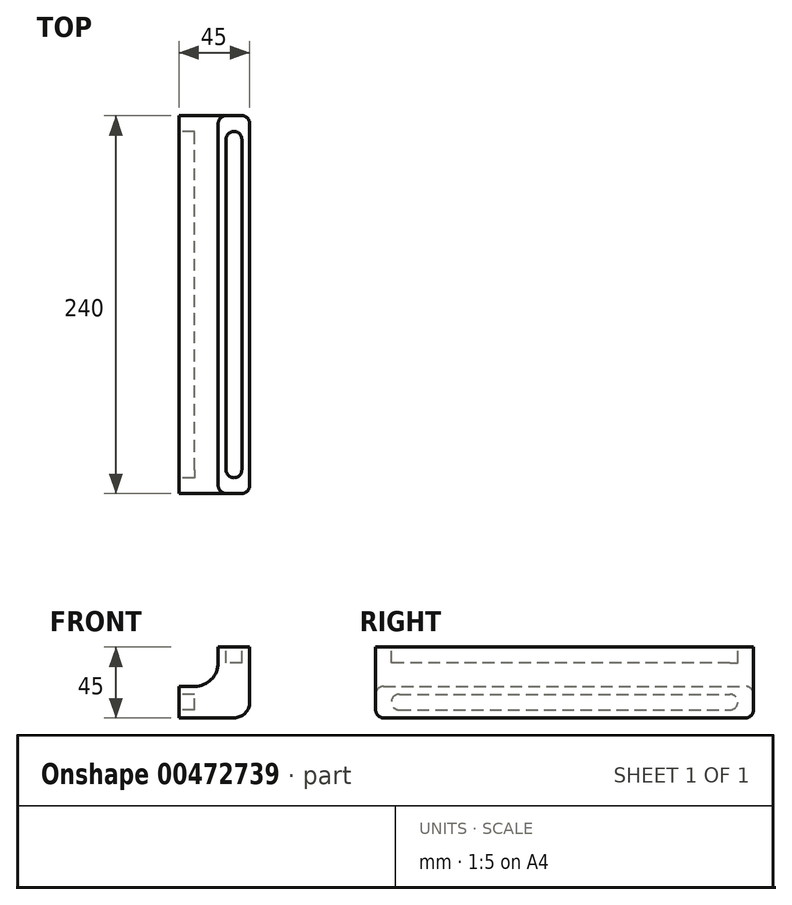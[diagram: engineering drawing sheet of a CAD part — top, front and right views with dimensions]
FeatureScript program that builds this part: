
annotation { "Feature Type Name" : "Feature", "Feature Type Description" : "" }
export const myFeature = defineFeature(function(context is Context, id is Id, definition is map)
    precondition{}
    {
        {
            var Q0;
            Q0=qCreatedBy(makeId("Front.planeOp"),FACE);
            var sketch = newSketch(context, id + "F0", { "sketchPlane" : qUnion([Q0])});
            skLineSegment(sketch, "E0.bottom", {"start": v(22.5, -22.5) * mm, "end": v(-22.5, -22.5) * mm});
            skLineSegment(sketch, "E0.top", {"start": v(22.5, 22.5) * mm, "end": v(2.5, 22.5) * mm});
            skLineSegment(sketch, "E0.left", {"start": v(22.5, -22.5) * mm, "end": v(22.5, 22.5) * mm});
            skLineSegment(sketch, "E0.right", {"start": v(-22.5, -22.5) * mm, "end": v(-22.5, -2.5) * mm});
            skPoint(sketch, "E0.middle", {"position": v(0, 0) * mm});
            skLineSegment(sketch, "E1", {"start": v(0, 22.5) * mm, "end": v(0, -22.5) * mm, "construction": true});
            skLineSegment(sketch, "E2", {"start": v(-22.5, 0) * mm, "end": v(22.5, 0) * mm, "construction": true});
            skLineSegment(sketch, "E3.0", {"start": v(2.5, -2.5) * mm, "end": v(-22.5, -2.5) * mm});
            skPoint(sketch, "E4.orphan", {"position": v(-22.5, 22.5) * mm});
            skLineSegment(sketch, "E5.trimOffspring", {"start": v(2.5, -2.5) * mm, "end": v(2.5, 22.5) * mm});
            skSolve(sketch);
        }
        {
            var Q0;
            Q0 = qSketchRegion(id + "F0", true);
            extrude(context, id + "F1", {"entities" : qUnion([Q0]), "depth" : 240 * mm, "offsetDistance" : 25 * mm});
        }
        {
            var Q0;
            Q0=makeQuery(id+"F1.opExtrude","SWEPT_EDGE",EDGE,{"disambiguationData":[OSD([sQuery(id+"F0.wireOp",EDGE,"E3.0"),sQuery(id+"F0.wireOp",EDGE,"E5.trimOffspring")])]});
            fillet(context, id + "F2", {"entities" : qUnion([Q0]), "radius" : 15 * mm, "tangentPropagation" : true, "allowEdgeOverflow" : false});
        }
        {
            var Q0;
            Q0=makeQuery(id+"F1.opExtrude","SWEPT_EDGE",EDGE,{"disambiguationData":[OSD([sQuery(id+"F0.wireOp",EDGE,"E0.bottom"),sQuery(id+"F0.wireOp",EDGE,"E0.left")])]});
            fillet(context, id + "F3", {"entities" : qUnion([Q0]), "radius" : 10 * mm, "tangentPropagation" : true, "allowEdgeOverflow" : false});
        }
        {
            var Q0;
            Q0=makeQuery(id+"F1.opExtrude","SWEPT_FACE",FACE,{"disambiguationData":[OSD([sQuery(id+"F0.wireOp",EDGE,"E0.top")])]});
            var sketch = newSketch(context, id + "F4", { "sketchPlane" : qUnion([Q0])});
            skLineSegment(sketch, "E6", {"start": v(12.5, -240) * mm, "end": v(12.5, 0) * mm, "construction": true});
            skLineSegment(sketch, "E7", {"start": v(2.5, -120) * mm, "end": v(22.5, -120) * mm, "construction": true});
            skArc(sketch, "E8", {"start": v(7.5, -225) * mm, "mid": v(12.5, -230) * mm, "end": v(17.5, -225) * mm});
            skArc(sketch, "E9.MirrorC", {"start": v(7.5, -15) * mm, "mid": v(12.5, -10) * mm, "end": v(17.5, -15) * mm});
            skLineSegment(sketch, "E10", {"start": v(7.5, -15) * mm, "end": v(7.5, -225) * mm});
            skLineSegment(sketch, "E11.MirrorCS", {"start": v(17.5, -15) * mm, "end": v(17.5, -225) * mm});
            skSolve(sketch);
        }
        {
            var Q0;
            Q0 = qSketchRegion(id + "F4", true);
            extrude(context, id + "F5", {"entities" : qUnion([Q0]), "operationType" : NewBodyOperationType.REMOVE, "oppositeDirection" : true, "depth" : 10 * mm, "offsetDistance" : 25 * mm});
        }
        {
            var Q0;
            Q0=makeQuery(id+"F1.opExtrude","SWEPT_FACE",FACE,{"disambiguationData":[OSD([sQuery(id+"F0.wireOp",EDGE,"E0.right")])]});
            var sketch = newSketch(context, id + "F6", { "sketchPlane" : qUnion([Q0])});
            skLineSegment(sketch, "E12", {"start": v(240, -12.5) * mm, "end": v(0, -12.5) * mm, "construction": true});
            skLineSegment(sketch, "E13", {"start": v(120, -2.5) * mm, "end": v(120, -22.5) * mm, "construction": true});
            skArc(sketch, "E14", {"start": v(15, -7.5) * mm, "mid": v(10, -12.5) * mm, "end": v(15, -17.5) * mm});
            skArc(sketch, "E15.MirrorC", {"start": v(225, -7.5) * mm, "mid": v(230, -12.5) * mm, "end": v(225, -17.5) * mm});
            skLineSegment(sketch, "E16", {"start": v(225, -7.5) * mm, "end": v(15, -7.5) * mm});
            skLineSegment(sketch, "E17.MirrorCS", {"start": v(225, -17.5) * mm, "end": v(15, -17.5) * mm});
            skSolve(sketch);
        }
        {
            var Q0;
            Q0 = qSketchRegion(id + "F6", true);
            extrude(context, id + "F7", {"entities" : qUnion([Q0]), "operationType" : NewBodyOperationType.REMOVE, "oppositeDirection" : true, "depth" : 10 * mm, "offsetDistance" : 25 * mm});
        }
        {
            var Q0;
            Q0=makeQuery(id+"F1.opExtrude","CAP_EDGE",EDGE,{"disambiguationData":[OSD([sQuery(id+"F0.wireOp",EDGE,"E0.left")])],"isStart":false});
            var Q1;
            {var subQ0=sQuery(id+"F0.wireOp",EDGE,"E0.left");var subQ1=sQuery(id+"F0.wireOp",EDGE,"E0.bottom");Q1=makeQuery(id+"F3.opFillet","BLEND_EDGE",EDGE,{"blendedFrom":[makeQuery(id+"F1.opExtrude","SWEPT_EDGE",EDGE,{"disambiguationData":[OSD([subQ1,subQ0])]}),makeQuery(id+"F1.opExtrude","CAP_FACE",FACE,{"disambiguationData":[OSD([subQ1,sQuery(id+"F0.wireOp",EDGE,"E0.top"),subQ0,sQuery(id+"F0.wireOp",EDGE,"E0.right"),sQuery(id+"F0.wireOp",EDGE,"E3.0"),sQuery(id+"F0.wireOp",EDGE,"E5.trimOffspring")])],"isStart":false})],"blendedInto":[makeQuery(id+"F1.opExtrude","CAP_FACE",FACE,{"disambiguationData":[OSD([subQ1,sQuery(id+"F0.wireOp",EDGE,"E0.top"),subQ0,sQuery(id+"F0.wireOp",EDGE,"E0.right"),sQuery(id+"F0.wireOp",EDGE,"E3.0"),sQuery(id+"F0.wireOp",EDGE,"E5.trimOffspring")])],"isStart":false})]});}
            fillet(context, id + "F8", {"entities" : qUnion([Q0, Q1]), "radius" : 5 * mm, "tangentPropagation" : true, "allowEdgeOverflow" : false});
        }
        {
            var Q0;
            Q0=makeQuery(id+"F1.opExtrude","CAP_EDGE",EDGE,{"disambiguationData":[OSD([sQuery(id+"F0.wireOp",EDGE,"E0.left")])],"isStart":true});
            fillet(context, id + "F9", {"entities" : qUnion([Q0]), "radius" : 5 * mm, "tangentPropagation" : true, "allowEdgeOverflow" : false});
        }
        {
            var Q0;
            {var subQ0=sQuery(id+"F0.wireOp",EDGE,"E5.trimOffspring");var subQ1=sQuery(id+"F0.wireOp",EDGE,"E3.0");Q0=makeQuery(id+"F2.opFillet","BLEND_EDGE",EDGE,{"blendedFrom":[makeQuery(id+"F1.opExtrude","SWEPT_EDGE",EDGE,{"disambiguationData":[OSD([subQ1,subQ0])]}),makeQuery(id+"F1.opExtrude","CAP_FACE",FACE,{"disambiguationData":[OSD([sQuery(id+"F0.wireOp",EDGE,"E0.bottom"),sQuery(id+"F0.wireOp",EDGE,"E0.top"),sQuery(id+"F0.wireOp",EDGE,"E0.left"),sQuery(id+"F0.wireOp",EDGE,"E0.right"),subQ1,subQ0])],"isStart":false})],"blendedInto":[makeQuery(id+"F1.opExtrude","CAP_FACE",FACE,{"disambiguationData":[OSD([sQuery(id+"F0.wireOp",EDGE,"E0.bottom"),sQuery(id+"F0.wireOp",EDGE,"E0.top"),sQuery(id+"F0.wireOp",EDGE,"E0.left"),sQuery(id+"F0.wireOp",EDGE,"E0.right"),subQ1,subQ0])],"isStart":false})]});}
            var Q1;
            {var subQ0=sQuery(id+"F0.wireOp",EDGE,"E5.trimOffspring");var subQ1=sQuery(id+"F0.wireOp",EDGE,"E3.0");Q1=makeQuery(id+"F2.opFillet","BLEND_EDGE",EDGE,{"blendedFrom":[makeQuery(id+"F1.opExtrude","SWEPT_EDGE",EDGE,{"disambiguationData":[OSD([subQ1,subQ0])]}),makeQuery(id+"F1.opExtrude","CAP_FACE",FACE,{"disambiguationData":[OSD([sQuery(id+"F0.wireOp",EDGE,"E0.bottom"),sQuery(id+"F0.wireOp",EDGE,"E0.top"),sQuery(id+"F0.wireOp",EDGE,"E0.left"),sQuery(id+"F0.wireOp",EDGE,"E0.right"),subQ1,subQ0])],"isStart":true})],"blendedInto":[makeQuery(id+"F1.opExtrude","CAP_FACE",FACE,{"disambiguationData":[OSD([sQuery(id+"F0.wireOp",EDGE,"E0.bottom"),sQuery(id+"F0.wireOp",EDGE,"E0.top"),sQuery(id+"F0.wireOp",EDGE,"E0.left"),sQuery(id+"F0.wireOp",EDGE,"E0.right"),subQ1,subQ0])],"isStart":true})]});}
            fillet(context, id + "F10", {"entities" : qUnion([Q0, Q1]), "radius" : 5 * mm, "tangentPropagation" : true, "allowEdgeOverflow" : false});
        }
    });
